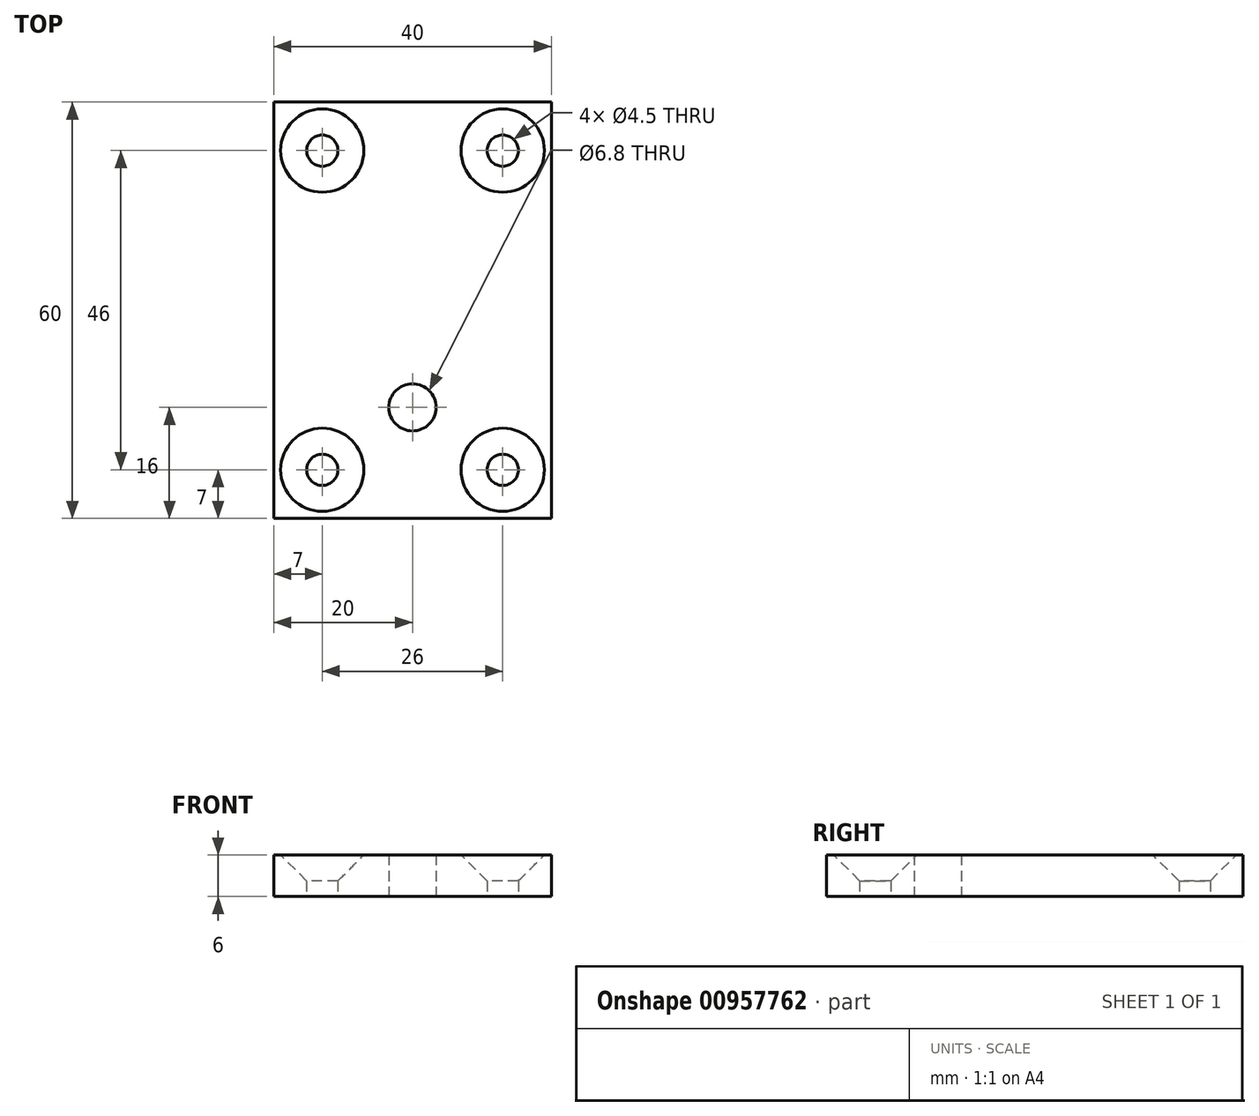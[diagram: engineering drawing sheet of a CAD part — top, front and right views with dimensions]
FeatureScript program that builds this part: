
annotation { "Feature Type Name" : "Feature", "Feature Type Description" : "" }
export const myFeature = defineFeature(function(context is Context, id is Id, definition is map)
    precondition{}
    {
        {
            var Q0;
            Q0=qCreatedBy(makeId("Top.planeOp"),FACE);
            var sketch = newSketch(context, id + "F0", { "sketchPlane" : qUnion([Q0])});
            skLineSegment(sketch, "E0.bottom", {"start": v(0, 0) * mm, "end": v(40, 0) * mm});
            skLineSegment(sketch, "E0.top", {"start": v(0, 60) * mm, "end": v(40, 60) * mm});
            skLineSegment(sketch, "E0.left", {"start": v(0, 0) * mm, "end": v(0, 60) * mm});
            skLineSegment(sketch, "E0.right", {"start": v(40, 0) * mm, "end": v(40, 60) * mm});
            skCircle(sketch, "E1", {"center": v(20, 16) * mm, "radius": 3.4 * mm});
            skLineSegment(sketch, "E2", {"start": v(20, 69.57) * mm, "end": v(20, -9.81) * mm, "construction": true});
            skCircle(sketch, "E3", {"center": v(33, 53) * mm, "radius": 2.25 * mm});
            skCircle(sketch, "E4", {"center": v(7, 53) * mm, "radius": 2.25 * mm});
            skCircle(sketch, "E5", {"center": v(7, 7) * mm, "radius": 2.25 * mm});
            skCircle(sketch, "E6", {"center": v(33, 7) * mm, "radius": 2.25 * mm});
            skSolve(sketch);
        }
        {
            var Q0;
            Q0=makeQuery(id+"F0.imprint","IMPRINT",FACE,{"disambiguationData":[TD([[makeQuery(id+"F0.imprint","IMPRINT",EDGE,{"derivedFrom":sQuery(id+"F0.wireOp",EDGE,"E0.bottom")}),1.0]])]});
            extrude(context, id + "F1", {"entities" : qUnion([Q0]), "depth" : 6 * mm, "offsetDistance" : 25 * mm});
        }
        {
            var Q0;
            Q0=makeQuery(id+"F1.opExtrude","CAP_EDGE",EDGE,{"disambiguationData":[OSD([sQuery(id+"F0.wireOp",EDGE,"E6")])],"isStart":false});
            var Q1;
            Q1=makeQuery(id+"F1.opExtrude","CAP_EDGE",EDGE,{"disambiguationData":[OSD([sQuery(id+"F0.wireOp",EDGE,"E5")])],"isStart":false});
            var Q2;
            Q2=makeQuery(id+"F1.opExtrude","CAP_EDGE",EDGE,{"disambiguationData":[OSD([sQuery(id+"F0.wireOp",EDGE,"E4")])],"isStart":false});
            var Q3;
            Q3=makeQuery(id+"F1.opExtrude","CAP_EDGE",EDGE,{"disambiguationData":[OSD([sQuery(id+"F0.wireOp",EDGE,"E3")])],"isStart":false});
            chamfer(context, id + "F2", {"entities" : qUnion([Q0, Q1, Q2, Q3]), "chamferType" : ChamferType.OFFSET_ANGLE, "width" : 3.75 * mm, "oppositeDirection" : false, "angle" : 45 * degree, "tangentPropagation" : true});
        }
    });
